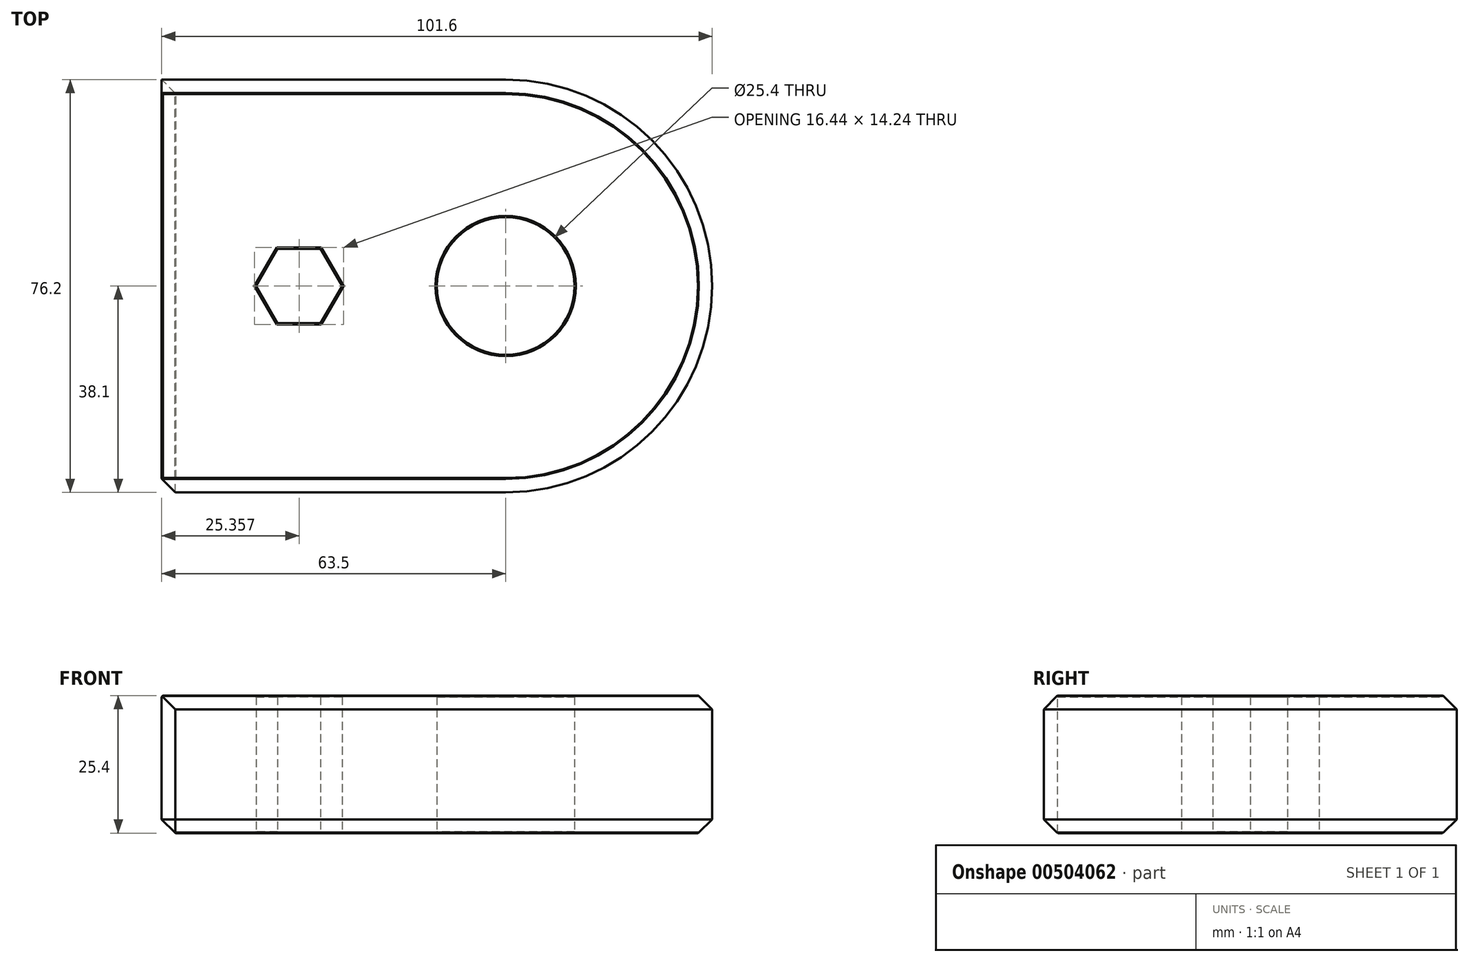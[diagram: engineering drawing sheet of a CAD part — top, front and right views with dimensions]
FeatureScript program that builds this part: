
annotation { "Feature Type Name" : "Feature", "Feature Type Description" : "" }
export const myFeature = defineFeature(function(context is Context, id is Id, definition is map)
    precondition{}
    {
        {
            var Q0;
            Q0=qCreatedBy(makeId("Right.planeOp"),FACE);
            var sketch = newSketch(context, id + "F0", { "sketchPlane" : qUnion([Q0])});
            skLineSegment(sketch, "E0.bottom", {"start": v(-38.1, -12.5) * mm, "end": v(38.1, -12.5) * mm});
            skLineSegment(sketch, "E0.top", {"start": v(-38.1, -37.9) * mm, "end": v(38.1, -37.9) * mm});
            skLineSegment(sketch, "E0.left", {"start": v(-38.1, -12.5) * mm, "end": v(-38.1, -37.9) * mm});
            skLineSegment(sketch, "E0.right", {"start": v(38.1, -12.5) * mm, "end": v(38.1, -37.9) * mm});
            skSolve(sketch);
        }
        {
            var Q0;
            Q0 = qSketchRegion(id + "F0", true);
            extrude(context, id + "F1", {"entities" : qUnion([Q0]), "depth" : 101.6 * mm});
        }
        {
            var Q0;
            Q0=makeQuery(id+"F1.opExtrude","SWEPT_FACE",FACE,{"disambiguationData":[OSD([sQuery(id+"F0.wireOp",EDGE,"E0.top")])]});
            var sketch = newSketch(context, id + "F2", { "sketchPlane" : qUnion([Q0])});
            skCircle(sketch, "E1", {"center": v(63.5, 0) * mm, "radius": 12.7 * mm});
            skSolve(sketch);
        }
        {
            var Q0;
            Q0=makeQuery(id+"F2.imprint","IMPRINT",FACE,{"disambiguationData":[TD([[makeQuery(id+"F2.imprint","IMPRINT",EDGE,{"derivedFrom":sQuery(id+"F2.wireOp",EDGE,"E1")}),-1.0]])]});
            extrude(context, id + "F3", {"entities" : qUnion([Q0]), "operationType" : NewBodyOperationType.INTERSECT, "oppositeDirection" : true, "depth" : 25.4 * mm});
        }
        {
            var Q0;
            Q0=makeQuery(id+"F1.opExtrude","CAP_EDGE",EDGE,{"disambiguationData":[OSD([sQuery(id+"F0.wireOp",EDGE,"E0.right")])],"isStart":false});
            var Q1;
            Q1=makeQuery(id+"F1.opExtrude","CAP_EDGE",EDGE,{"disambiguationData":[OSD([sQuery(id+"F0.wireOp",EDGE,"E0.left")])],"isStart":false});
            fillet(context, id + "F4", {"entities" : qUnion([Q0, Q1]), "radius" : 38.1 * mm, "tangentPropagation" : true, "allowEdgeOverflow" : false});
        }
        {
            var Q0;
            Q0=makeQuery(id+"F4.opFillet","BLEND_EDGE",EDGE,{"blendedFrom":[makeQuery(id+"F1.opExtrude","CAP_EDGE",EDGE,{"disambiguationData":[OSD([sQuery(id+"F0.wireOp",EDGE,"E0.left")])],"isStart":false}),makeQuery(id+"F1.opExtrude","SWEPT_FACE",FACE,{"disambiguationData":[OSD([sQuery(id+"F0.wireOp",EDGE,"E0.top")])]})],"blendedInto":[makeQuery(id+"F1.opExtrude","SWEPT_FACE",FACE,{"disambiguationData":[OSD([sQuery(id+"F0.wireOp",EDGE,"E0.top")])]})]});
            var Q1;
            Q1=makeQuery(id+"F1.opExtrude","SWEPT_EDGE",EDGE,{"disambiguationData":[OSD([sQuery(id+"F0.wireOp",EDGE,"E0.top"),sQuery(id+"F0.wireOp",EDGE,"E0.right")])]});
            var Q2;
            Q2=makeQuery(id+"F1.opExtrude","SWEPT_EDGE",EDGE,{"disambiguationData":[OSD([sQuery(id+"F0.wireOp",EDGE,"E0.bottom"),sQuery(id+"F0.wireOp",EDGE,"E0.right")])]});
            var Q3;
            Q3=makeQuery(id+"F4.opFillet","BLEND_EDGE",EDGE,{"blendedFrom":[makeQuery(id+"F1.opExtrude","CAP_EDGE",EDGE,{"disambiguationData":[OSD([sQuery(id+"F0.wireOp",EDGE,"E0.left")])],"isStart":false}),makeQuery(id+"F1.opExtrude","SWEPT_FACE",FACE,{"disambiguationData":[OSD([sQuery(id+"F0.wireOp",EDGE,"E0.bottom")])]})],"blendedInto":[makeQuery(id+"F1.opExtrude","SWEPT_FACE",FACE,{"disambiguationData":[OSD([sQuery(id+"F0.wireOp",EDGE,"E0.bottom")])]})]});
            var Q4;
            Q4=makeQuery(id+"F1.opExtrude","SWEPT_EDGE",EDGE,{"disambiguationData":[OSD([sQuery(id+"F0.wireOp",EDGE,"E0.bottom"),sQuery(id+"F0.wireOp",EDGE,"E0.left")])]});
            var Q5;
            Q5=makeQuery(id+"F1.opExtrude","SWEPT_EDGE",EDGE,{"disambiguationData":[OSD([sQuery(id+"F0.wireOp",EDGE,"E0.top"),sQuery(id+"F0.wireOp",EDGE,"E0.left")])]});
            var Q6;
            Q6=makeQuery(id+"F1.opExtrude","CAP_EDGE",EDGE,{"disambiguationData":[OSD([sQuery(id+"F0.wireOp",EDGE,"E0.top")])],"isStart":true});
            var Q7;
            Q7=makeQuery(id+"F1.opExtrude","CAP_EDGE",EDGE,{"disambiguationData":[OSD([sQuery(id+"F0.wireOp",EDGE,"E0.left")])],"isStart":true});
            var Q8;
            Q8=makeQuery(id+"F3.boolean.opBoolean","COPY",EDGE,{"derivedFrom":makeQuery(id+"F3.boolean.toolComplement.opBoolean","COPY",EDGE,{"derivedFrom":makeQuery(id+"F3.opExtrude","CAP_EDGE",EDGE,{"disambiguationData":[OSD([sQuery(id+"F2.wireOp",EDGE,"E1")])],"isStart":true})})});
            chamfer(context, id + "F5", {"entities" : qUnion([Q0, Q1, Q2, Q3, Q4, Q5, Q6, Q7, Q8]), "width" : 2.54 * mm, "tangentPropagation" : true});
        }
        {
            var Q0;
            Q0=makeQuery(id+"F1.opExtrude","SWEPT_FACE",FACE,{"disambiguationData":[OSD([sQuery(id+"F0.wireOp",EDGE,"E0.top")])]});
            var sketch = newSketch(context, id + "F6", { "sketchPlane" : qUnion([Q0])});
            skCircle(sketch, "E2.cCircle", {"center": v(25.36, 0) * mm, "radius": 6.87 * mm, "construction": true});
            skLineSegment(sketch, "E2.0", {"start": v(29.32, -6.87) * mm, "end": v(21.4, -6.87) * mm});
            skLineSegment(sketch, "E2.1", {"start": v(21.4, -6.87) * mm, "end": v(17.43, 0) * mm});
            skLineSegment(sketch, "E2.2", {"start": v(17.43, 0) * mm, "end": v(21.4, 6.87) * mm});
            skLineSegment(sketch, "E2.3", {"start": v(21.4, 6.87) * mm, "end": v(29.32, 6.87) * mm});
            skLineSegment(sketch, "E2.4", {"start": v(29.32, 6.87) * mm, "end": v(33.28, 0) * mm});
            skLineSegment(sketch, "E2.5", {"start": v(33.28, 0) * mm, "end": v(29.32, -6.87) * mm});
            skPoint(sketch, "E2.0.midPoint", {"position": v(25.36, -6.87) * mm});
            skSolve(sketch);
        }
        {
            var Q0;
            Q0 = qSketchRegion(id + "F6", true);
            extrude(context, id + "F7", {"entities" : qUnion([Q0]), "operationType" : NewBodyOperationType.REMOVE, "oppositeDirection" : true, "depth" : 25.4 * mm});
        }
        {
            var Q0;
            Q0=makeQuery(id+"F7.boolean.opBoolean","COPY",EDGE,{"derivedFrom":makeQuery(id+"F7.opExtrude","CAP_EDGE",EDGE,{"disambiguationData":[OSD([sQuery(id+"F6.wireOp",EDGE,"E2.2")])],"isStart":true})});
            var Q1;
            Q1=makeQuery(id+"F7.boolean.opBoolean","COPY",EDGE,{"derivedFrom":makeQuery(id+"F7.opExtrude","CAP_EDGE",EDGE,{"disambiguationData":[OSD([sQuery(id+"F6.wireOp",EDGE,"E2.1")])],"isStart":true})});
            var Q2;
            Q2=makeQuery(id+"F1.opExtrude","SWEPT_FACE",FACE,{"disambiguationData":[OSD([sQuery(id+"F0.wireOp",EDGE,"E0.top")])]});
            var Q3;
            Q3=makeQuery(id+"F1.opExtrude","SWEPT_FACE",FACE,{"disambiguationData":[OSD([sQuery(id+"F0.wireOp",EDGE,"E0.bottom")])]});
            chamfer(context, id + "F8", {"entities" : qUnion([Q0, Q1, Q2, Q3]), "width" : 0.25 * mm, "tangentPropagation" : true});
        }
    });
